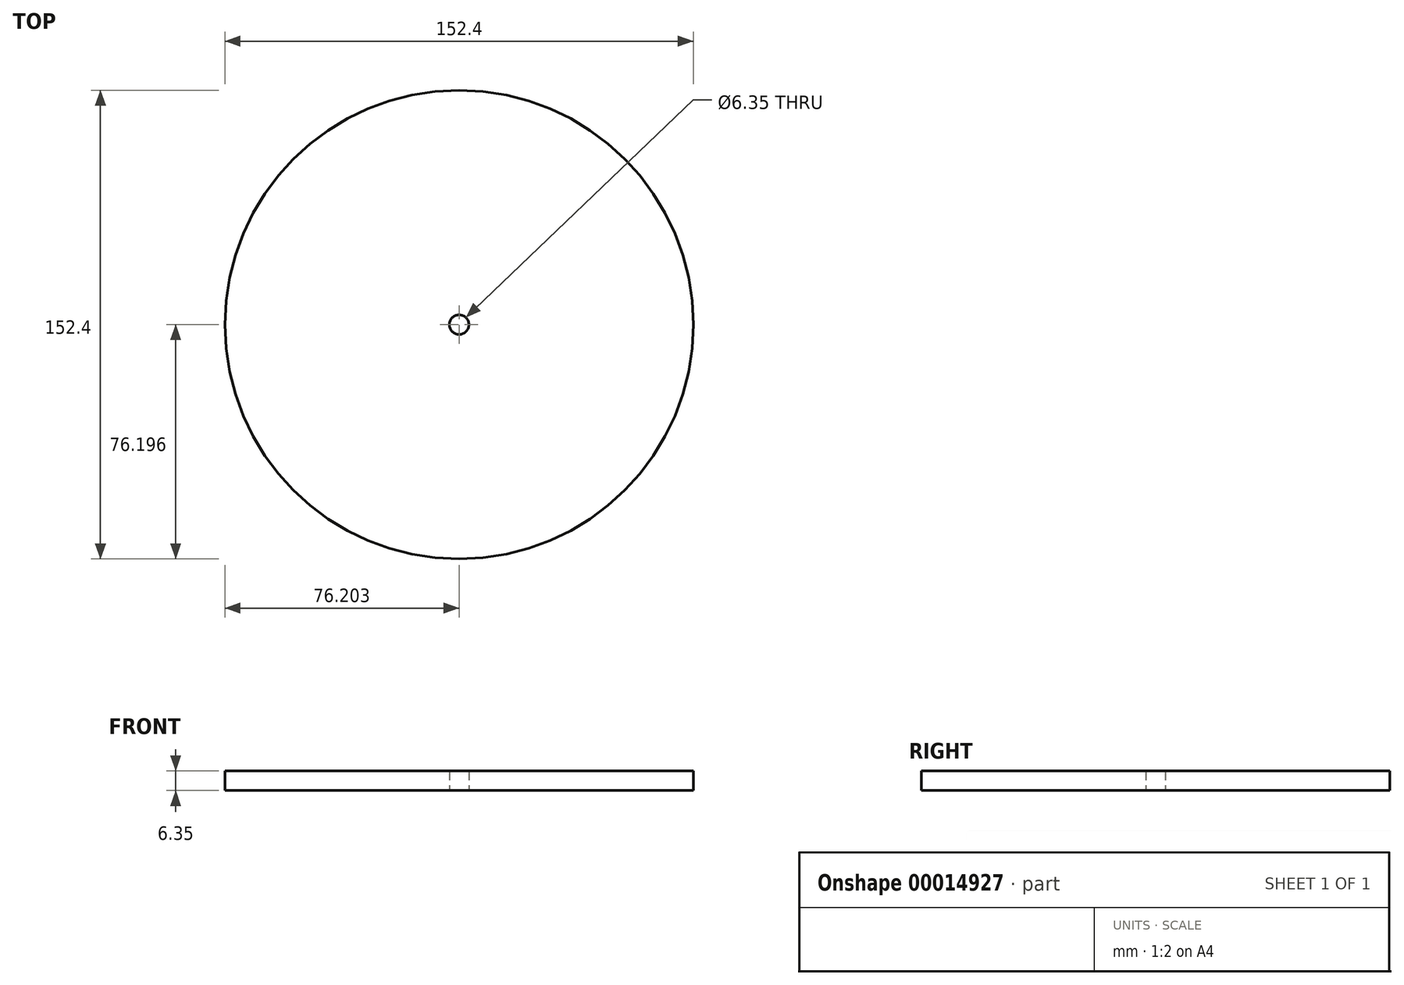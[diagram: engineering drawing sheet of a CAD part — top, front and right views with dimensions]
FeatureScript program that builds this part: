
annotation { "Feature Type Name" : "Feature", "Feature Type Description" : "" }
export const myFeature = defineFeature(function(context is Context, id is Id, definition is map)
    precondition{}
    {
        {
            var Q0;
            Q0=qCreatedBy(makeId("Top.planeOp"),FACE);
            var sketch = newSketch(context, id + "F0", { "sketchPlane" : qUnion([Q0])});
            skCircle(sketch, "E0", {"center": v(-45.45, 46.48) * mm, "radius": 76.2 * mm});
            skCircle(sketch, "E1", {"center": v(-45.45, 46.48) * mm, "radius": 3.18 * mm});
            skSolve(sketch);
        }
        {
            var Q0;
            Q0=makeQuery(id+"F0.imprint","IMPRINT",FACE,{"disambiguationData":[TD([[makeQuery(id+"F0.imprint","IMPRINT",EDGE,{"derivedFrom":sQuery(id+"F0.wireOp",EDGE,"E0")}),1.0]])]});
            extrude(context, id + "F1", {"entities" : qUnion([Q0]), "depth" : 6.35 * mm});
        }
    });
